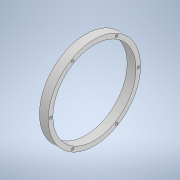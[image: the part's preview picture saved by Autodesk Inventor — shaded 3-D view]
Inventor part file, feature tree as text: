
AUTODESK INVENTOR PART (.ipt)
format: ipt  version: 2020 (Build 240168000, 168)  size: 145,408 bytes
history: native  units: mm
features: sketch x2, revolve x1, hole x1, pattern_circular x1, projected_geometry x1
ambient origin geometry x8: Origin, YZ Plane, XZ Plane, XY Plane, X Axis, Y Axis, Z Axis, Center Point
bodies: Solid1 (feature_tree)
feature tree (6):
  revolve  "Revolution1"  [1 undecoded]
  hole  "Hole1"  [1 undecoded]
  pattern_circular  "Circular Pattern1"  [2 undecoded]
  sketch  "Sketch1"  dims[d11=90.0deg d30=15.4mm]
  sketch  "Sketch2"  dims[d31=8.0mm d33=4.0mm d34=4.0mm d35=4.5mm d36=8.0mm d37=9.4mm d38=2.0mm d39=90.0deg d40=8.0mm d41=20.594885mm d42=60.0mm d43=360.0deg d45=80.5mm]
  projected_geometry  "Projected Loop1"
note: 4 required parameter values undecoded (feature->parameter linkage not recoverable at this tier; creation-order binding heuristic only, values carry confidence <= 0.55)